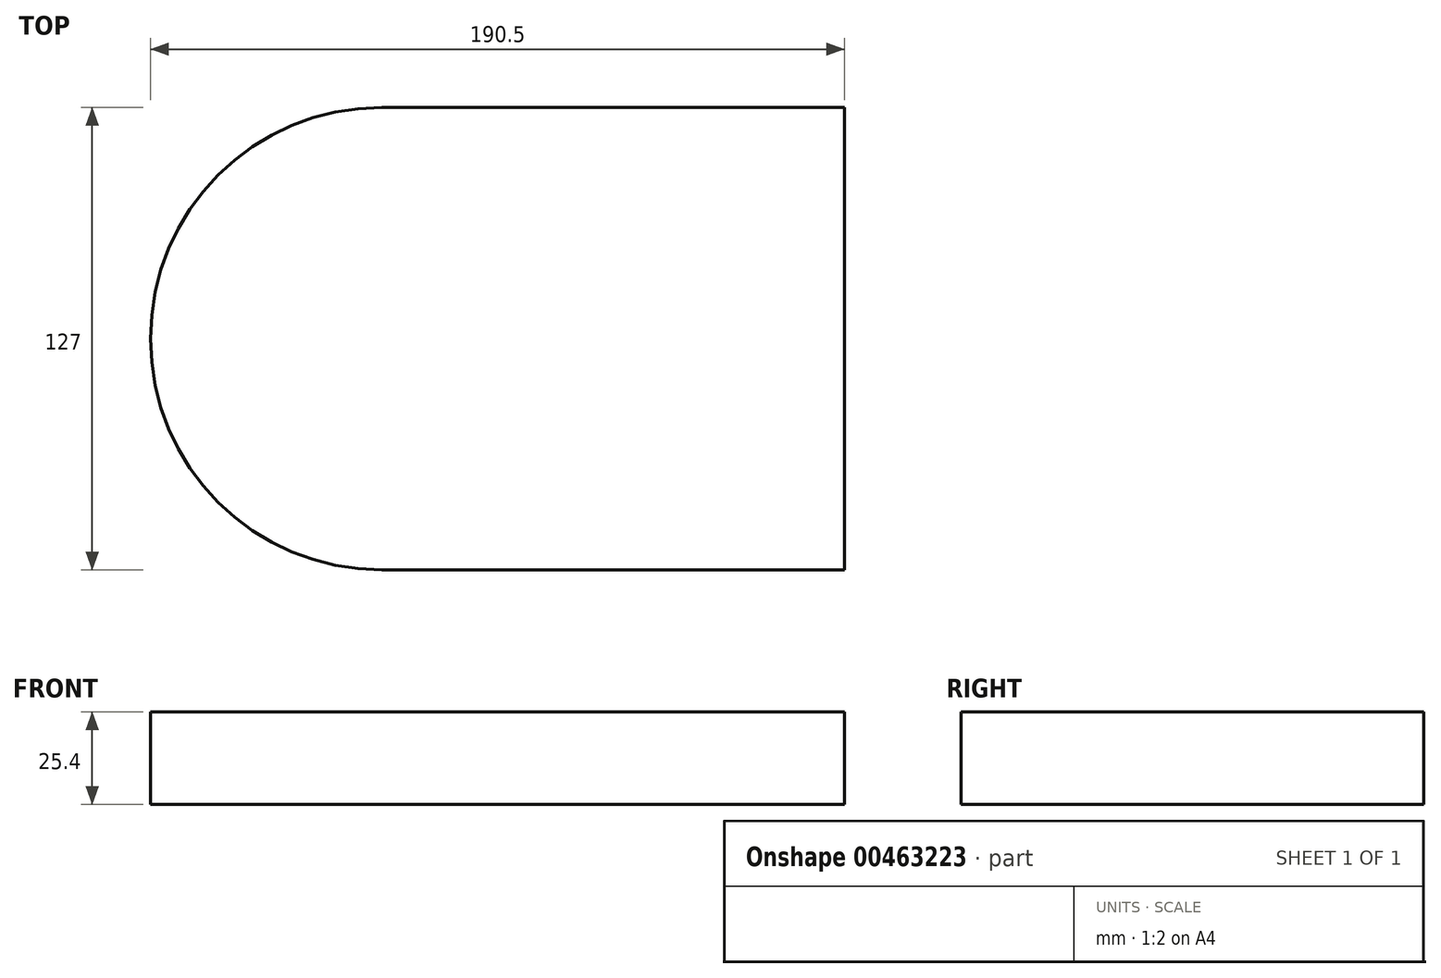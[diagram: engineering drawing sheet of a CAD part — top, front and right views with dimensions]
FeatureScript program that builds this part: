
annotation { "Feature Type Name" : "Feature", "Feature Type Description" : "" }
export const myFeature = defineFeature(function(context is Context, id is Id, definition is map)
    precondition{}
    {
        {
            var Q0;
            Q0=qCreatedBy(makeId("Top.planeOp"),FACE);
            var sketch = newSketch(context, id + "F0", { "sketchPlane" : qUnion([Q0])});
            skLineSegment(sketch, "E0.bottom", {"start": v(0, 0) * mm, "end": v(127, 0) * mm});
            skLineSegment(sketch, "E0.top", {"start": v(0, -127) * mm, "end": v(127, -127) * mm});
            skLineSegment(sketch, "E0.right", {"start": v(127, 0) * mm, "end": v(127, -127) * mm});
            skArc(sketch, "E1", {"start": v(0, -127) * mm, "mid": v(-63.5, -63.5) * mm, "end": v(0, 0) * mm});
            skSolve(sketch);
        }
        {
            var Q0;
            Q0 = qSketchRegion(id + "F0", true);
            extrude(context, id + "F1", {"entities" : qUnion([Q0]), "depth" : 25.4 * mm});
        }
    });
